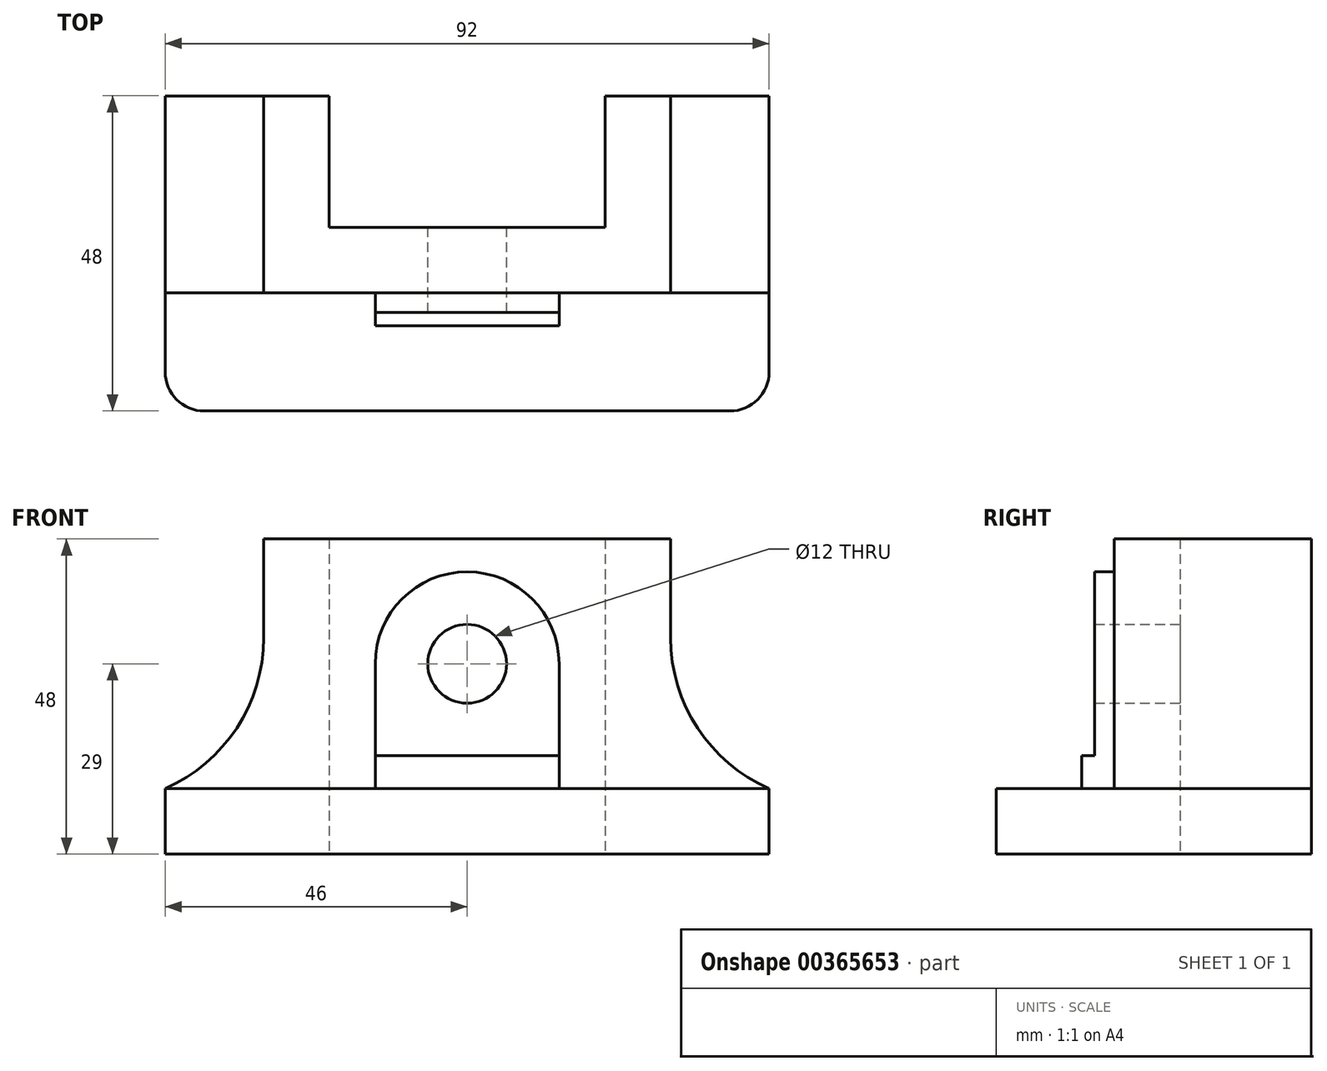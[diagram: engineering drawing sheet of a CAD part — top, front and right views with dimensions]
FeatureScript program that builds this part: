
annotation { "Feature Type Name" : "Feature", "Feature Type Description" : "" }
export const myFeature = defineFeature(function(context is Context, id is Id, definition is map)
    precondition{}
    {
        {
            var Q0;
            Q0=qCreatedBy(makeId("Top.planeOp"),FACE);
            var sketch = newSketch(context, id + "F0", { "sketchPlane" : qUnion([Q0])});
            skLineSegment(sketch, "E0", {"start": v(0, -1.62) * mm, "end": v(-21, -1.62) * mm});
            skLineSegment(sketch, "E1", {"start": v(-21, -1.62) * mm, "end": v(-21, 18.37) * mm});
            skLineSegment(sketch, "E2", {"start": v(-21, 18.37) * mm, "end": v(-31, 18.37) * mm});
            skLineSegment(sketch, "E3", {"start": v(-31, 18.37) * mm, "end": v(-31, -11.62) * mm});
            skLineSegment(sketch, "E4", {"start": v(-31, -11.63) * mm, "end": v(0, -11.62) * mm});
            skLineSegment(sketch, "E5", {"start": v(-31, 18.37) * mm, "end": v(-46, 18.37) * mm});
            skLineSegment(sketch, "E6", {"start": v(-46, 18.37) * mm, "end": v(-46, -29.62) * mm});
            skLineSegment(sketch, "E7", {"start": v(-46, -29.62) * mm, "end": v(0, -29.62) * mm});
            skLineSegment(sketch, "E8.MirrorCS", {"start": v(21, -1.62) * mm, "end": v(21, 18.37) * mm});
            skLineSegment(sketch, "E9.MirrorCS", {"start": v(46, -29.62) * mm, "end": v(0, -29.63) * mm});
            skLineSegment(sketch, "E10.MirrorCS", {"start": v(31, 18.38) * mm, "end": v(46, 18.38) * mm});
            skLineSegment(sketch, "E11.MirrorCS", {"start": v(46, 18.37) * mm, "end": v(46, -29.62) * mm});
            skLineSegment(sketch, "E12.MirrorCS", {"start": v(21, 18.37) * mm, "end": v(31, 18.38) * mm});
            skLineSegment(sketch, "E13.MirrorCS", {"start": v(0, -1.62) * mm, "end": v(21, -1.62) * mm});
            skLineSegment(sketch, "E14.MirrorCS", {"start": v(31, -11.62) * mm, "end": v(0, -11.62) * mm});
            skLineSegment(sketch, "E15.MirrorCS", {"start": v(31, 18.37) * mm, "end": v(31, -11.62) * mm});
            skSolve(sketch);
        }
        {
            var Q0;
            Q0=makeQuery(id+"F0.imprint","IMPRINT",FACE,{"disambiguationData":[TD([[makeQuery(id+"F0.imprint","IMPRINT",EDGE,{"derivedFrom":sQuery(id+"F0.wireOp",EDGE,"E0")}),1.0]])]});
            extrude(context, id + "F1", {"entities" : qUnion([Q0]), "depth" : 48 * mm});
        }
        {
            var Q0;
            Q0 = qSketchRegion(id + "F0", true);
            extrude(context, id + "F2", {"entities" : qUnion([Q0]), "operationType" : NewBodyOperationType.ADD, "depth" : 10 * mm});
        }
        {
            var Q0;
            Q0=makeQuery(id+"F2.opExtrude","SWEPT_EDGE",EDGE,{"disambiguationData":[OSD([sQuery(id+"F0.wireOp",EDGE,"E6"),sQuery(id+"F0.wireOp",EDGE,"E7")])]});
            var Q1;
            Q1=makeQuery(id+"F2.opExtrude","SWEPT_EDGE",EDGE,{"disambiguationData":[OSD([sQuery(id+"F0.wireOp",EDGE,"E9.MirrorCS"),sQuery(id+"F0.wireOp",EDGE,"E11.MirrorCS")])]});
            fillet(context, id + "F3", {"entities" : qUnion([Q0, Q1]), "radius" : 6 * mm, "tangentPropagation" : true, "allowEdgeOverflow" : false});
        }
        {
            var Q0;
            Q0=makeQuery(id+"F2.boolean.opBoolean","INTERSECT",EDGE,{"derivedFrom":[makeQuery(id+"F1.opExtrude","SWEPT_FACE",FACE,{"disambiguationData":[OSD([sQuery(id+"F0.wireOp",EDGE,"E15.MirrorCS")])]}),makeQuery(id+"F2.opExtrude","CAP_FACE",FACE,{"disambiguationData":[OSD([sQuery(id+"F0.wireOp",EDGE,"E0"),sQuery(id+"F0.wireOp",EDGE,"E1"),sQuery(id+"F0.wireOp",EDGE,"E2"),sQuery(id+"F0.wireOp",EDGE,"E5"),sQuery(id+"F0.wireOp",EDGE,"E6"),sQuery(id+"F0.wireOp",EDGE,"E7"),sQuery(id+"F0.wireOp",EDGE,"E8.MirrorCS"),sQuery(id+"F0.wireOp",EDGE,"E9.MirrorCS"),sQuery(id+"F0.wireOp",EDGE,"E10.MirrorCS"),sQuery(id+"F0.wireOp",EDGE,"E11.MirrorCS"),sQuery(id+"F0.wireOp",EDGE,"E12.MirrorCS"),sQuery(id+"F0.wireOp",EDGE,"E13.MirrorCS")])],"isStart":false})]});
            fillet(context, id + "F4", {"entities" : qUnion([Q0]), "radius" : 25 * mm, "tangentPropagation" : true, "allowEdgeOverflow" : false});
        }
        {
            var Q0;
            Q0=makeQuery(id+"F2.boolean.opBoolean","INTERSECT",EDGE,{"derivedFrom":[makeQuery(id+"F1.opExtrude","SWEPT_FACE",FACE,{"disambiguationData":[OSD([sQuery(id+"F0.wireOp",EDGE,"E3")])]}),makeQuery(id+"F2.opExtrude","CAP_FACE",FACE,{"disambiguationData":[OSD([sQuery(id+"F0.wireOp",EDGE,"E0"),sQuery(id+"F0.wireOp",EDGE,"E1"),sQuery(id+"F0.wireOp",EDGE,"E2"),sQuery(id+"F0.wireOp",EDGE,"E5"),sQuery(id+"F0.wireOp",EDGE,"E6"),sQuery(id+"F0.wireOp",EDGE,"E7"),sQuery(id+"F0.wireOp",EDGE,"E8.MirrorCS"),sQuery(id+"F0.wireOp",EDGE,"E9.MirrorCS"),sQuery(id+"F0.wireOp",EDGE,"E10.MirrorCS"),sQuery(id+"F0.wireOp",EDGE,"E11.MirrorCS"),sQuery(id+"F0.wireOp",EDGE,"E12.MirrorCS"),sQuery(id+"F0.wireOp",EDGE,"E13.MirrorCS")])],"isStart":false})]});
            fillet(context, id + "F5", {"entities" : qUnion([Q0]), "radius" : 25 * mm, "tangentPropagation" : true, "allowEdgeOverflow" : false});
        }
        {
            var Q0;
            Q0=makeQuery(id+"F1.opExtrude","SWEPT_FACE",FACE,{"disambiguationData":[OSD([sQuery(id+"F0.wireOp",EDGE,"E4"),sQuery(id+"F0.wireOp",EDGE,"E14.MirrorCS")])]});
            var sketch = newSketch(context, id + "F6", { "sketchPlane" : qUnion([Q0])});
            skLineSegment(sketch, "E16.top", {"start": v(-14, 10) * mm, "end": v(14, 10) * mm});
            skLineSegment(sketch, "E16.left", {"start": v(-14, 15) * mm, "end": v(-14, 10) * mm});
            skLineSegment(sketch, "E16.right", {"start": v(14, 15) * mm, "end": v(14, 10) * mm});
            skLineSegment(sketch, "E17", {"start": v(-14, 15) * mm, "end": v(0, 15) * mm});
            skLineSegment(sketch, "E18", {"start": v(0, 15) * mm, "end": v(14, 15) * mm});
            skLineSegment(sketch, "E19", {"start": v(-14, 15) * mm, "end": v(-14, 29) * mm});
            skLineSegment(sketch, "E20", {"start": v(14, 15) * mm, "end": v(14, 29) * mm});
            skArc(sketch, "E21", {"start": v(-14, 29) * mm, "mid": v(0, 43) * mm, "end": v(14, 29) * mm});
            skCircle(sketch, "E22", {"center": v(0, 29) * mm, "radius": 6 * mm});
            skSolve(sketch);
        }
        {
            var Q0;
            Q0=makeQuery(id+"F6.imprint","IMPRINT",FACE,{"disambiguationData":[TD([[makeQuery(id+"F6.imprint","IMPRINT",EDGE,{"derivedFrom":sQuery(id+"F6.wireOp",EDGE,"E16.left")}),1.0]])]});
            extrude(context, id + "F7", {"entities" : qUnion([Q0]), "operationType" : NewBodyOperationType.ADD, "depth" : 5 * mm});
        }
        {
            var Q0;
            Q0 = qSketchRegion(id + "F6", true);
            extrude(context, id + "F8", {"entities" : qUnion([Q0]), "operationType" : NewBodyOperationType.ADD, "depth" : 3 * mm});
        }
        {
            var Q0;
            Q0=makeQuery(id+"F8.boolean.opBoolean","SPLIT",FACE,{"disambiguationData":[TD([makeQuery(id+"F8.opExtrude","SWEPT_FACE",FACE,{"disambiguationData":[OSD([sQuery(id+"F6.wireOp",EDGE,"E22")])]})])],"derivedFrom":makeQuery(id+"F1.opExtrude","SWEPT_FACE",FACE,{"disambiguationData":[OSD([sQuery(id+"F0.wireOp",EDGE,"E4"),sQuery(id+"F0.wireOp",EDGE,"E14.MirrorCS")])]})});
            extrude(context, id + "F9", {"entities" : qUnion([Q0]), "operationType" : NewBodyOperationType.REMOVE, "oppositeDirection" : true, "depth" : 25 * mm});
        }
    });
